# Revit family: Haworth_Patterns_Bench
name_source: partatom
category: Furniture Systems
revit_build: Autodesk Revit 2018 (Build: 20170223_1515(x64)
units: mm (PartAtom-declared; Revit-internal decimal feet)

## family parameters
Always vertical = Yes
Cut with Voids When Loaded = No
OmniClass Number = 23.40.70.14.64.21
OmniClass Title = Systems Furniture
Part Type = Normal
Room Calculation Point = No
Round Connector Dimension = Use Diameter
Shared = No
Work Plane-Based = No

## types (6) — shared parameters
Actual Height = 17"
Assembly Code = E2020200
Bench Finish = Haworth _ Wood _ White Oak
Cushion Finish = Haworth _ Fabric _ Tellure _ Ivory 3A-35
Custom Size = No
Description = Haworth - Patterns Bench
Flip Top = Yes
Flip Top Finish = Haworth _ Paint _ Metallic Champagne
Manufacturer = Haworth
Max. Depth = 30"
Max. Width = 126"
Min. Depth = 22"
Min. Width = 78"
Model = Haworth - Patterns Bench
Revision Number = 3
Shelf = Yes
Size = Verify Final Dim. w/ Haworth
Standard Depths = 22, 30 in.
Standard Width = 78, 102, 126 in.
Sustainability Info = http://www.haworth.com
URL = https://www.haworth.com
URL - Product = https://www.haworth.com
Warranty = http://www.haworth.com

## per-type parameters (varying)
| type | Actual Depth | Actual Width | Cushion | Cushion Depth | Depth | Left Cushion | Left Cushion Width | Power Location | Right Cushion | Right Cushion Width | Width |
| 78w 22d | 22" | 78" | Yes | 21" | 22" | No | 24 1/2" | 12 1/2" | Yes | 52 1/2" | 78" |
| 78w 30d | 30" | 78" | Yes | 29" | 30" | No | 24 1/2" | 12 1/2" | Yes | 52 1/2" | 78" |
| 102w 22d | 22" | 102" | No | 21" | 22" | No | 36 1/2" | 51" | No | 36 1/2" | 102" |
| 126w 22d | 22" | 126" | Yes | 21" | 22" | Yes | 48 1/2" | 63" | Yes | 48 1/2" | 126" |
| 126w 30d | 30" | 126" | Yes | 29" | 30" | Yes | 48 1/2" | 63" | Yes | 48 1/2" | 126" |
| 102w 30d | 30" | 102" | Yes | 29" | 30" | Yes | 36 1/2" | 51" | Yes | 36 1/2" | 102" |

## geometry (parser evidence)
native form markers: Sweep x9
no freeform markers — native parametric forms only
